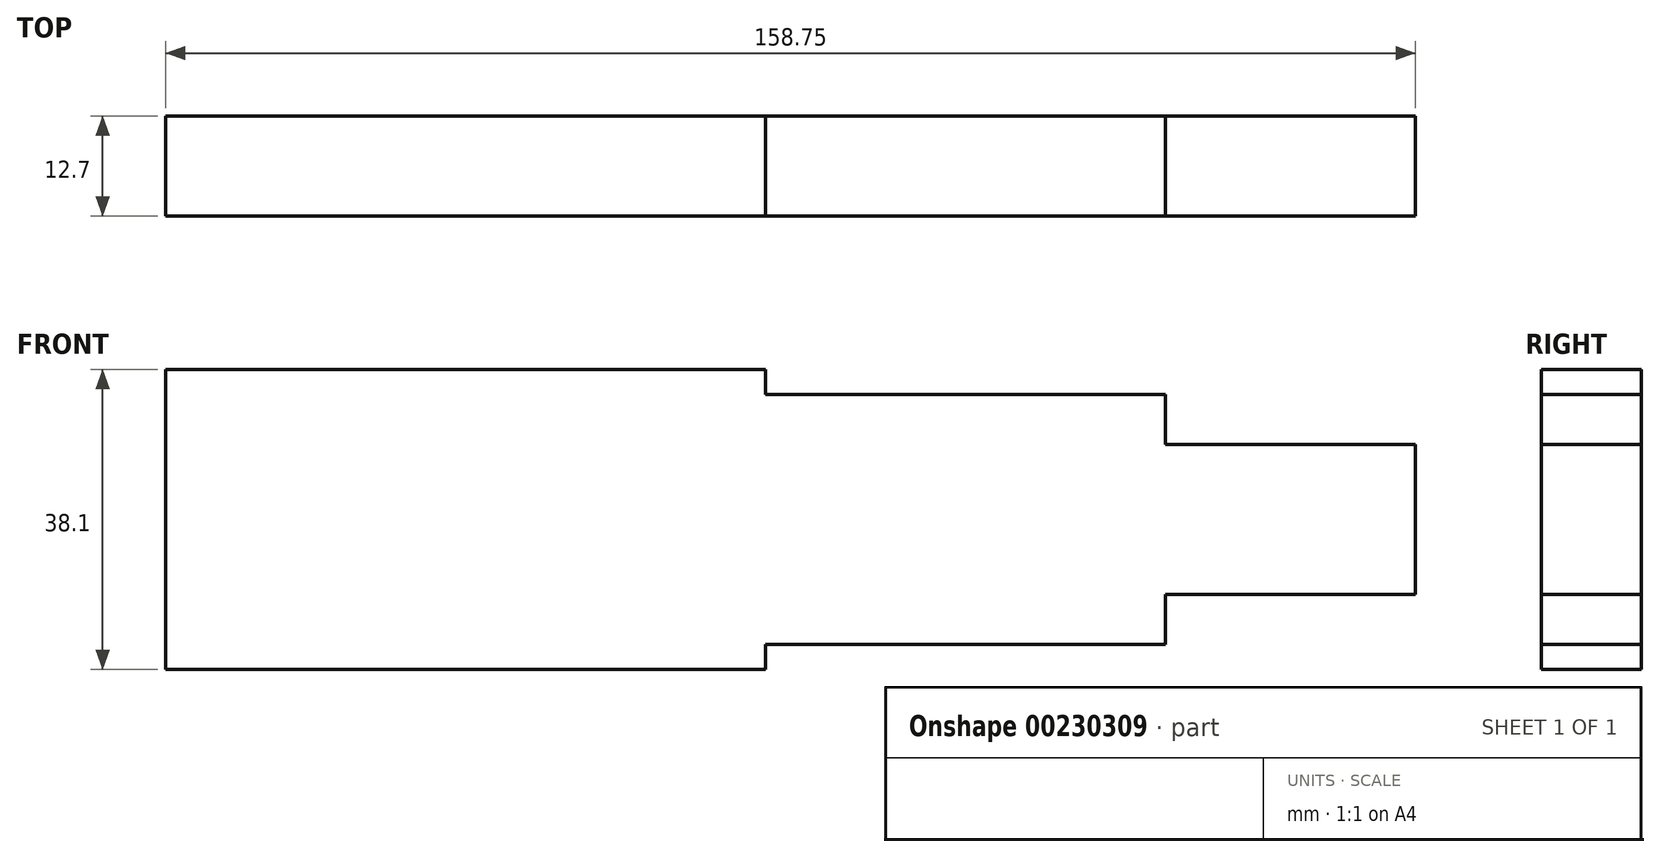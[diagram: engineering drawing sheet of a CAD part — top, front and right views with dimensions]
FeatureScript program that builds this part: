
annotation { "Feature Type Name" : "Feature", "Feature Type Description" : "" }
export const myFeature = defineFeature(function(context is Context, id is Id, definition is map)
    precondition{}
    {
        {
            var Q0;
            Q0=qCreatedBy(makeId("Front.planeOp"),FACE);
            var sketch = newSketch(context, id + "F0", { "sketchPlane" : qUnion([Q0])});
            skLineSegment(sketch, "E0.bottom", {"start": v(0, 0) * mm, "end": v(76.2, 0) * mm});
            skLineSegment(sketch, "E0.top", {"start": v(0, 38.1) * mm, "end": v(76.2, 38.1) * mm});
            skLineSegment(sketch, "E0.left", {"start": v(0, 0) * mm, "end": v(0, 38.1) * mm});
            skLineSegment(sketch, "E0.right", {"start": v(76.2, 0) * mm, "end": v(76.2, 3.17) * mm});
            skLineSegment(sketch, "E1.bottom", {"start": v(76.2, 34.93) * mm, "end": v(127, 34.93) * mm});
            skLineSegment(sketch, "E1.top", {"start": v(76.2, 3.17) * mm, "end": v(127, 3.17) * mm});
            skLineSegment(sketch, "E1.right", {"start": v(127, 34.93) * mm, "end": v(127, 28.58) * mm});
            skLineSegment(sketch, "E2.bottom", {"start": v(127, 28.58) * mm, "end": v(158.75, 28.58) * mm});
            skLineSegment(sketch, "E2.top", {"start": v(127, 9.53) * mm, "end": v(158.75, 9.53) * mm});
            skLineSegment(sketch, "E2.right", {"start": v(158.75, 28.58) * mm, "end": v(158.75, 9.53) * mm});
            skLineSegment(sketch, "E3.trimOffspring", {"start": v(76.2, 34.93) * mm, "end": v(76.2, 38.1) * mm});
            skLineSegment(sketch, "E4.trimOffspring", {"start": v(127, 9.53) * mm, "end": v(127, 3.17) * mm});
            skSolve(sketch);
        }
        {
            var Q0;
            Q0=makeQuery(id+"F0.imprint","IMPRINT",FACE,{"disambiguationData":[TD([[makeQuery(id+"F0.imprint","IMPRINT",EDGE,{"derivedFrom":sQuery(id+"F0.wireOp",EDGE,"E0.bottom")}),1.0]])]});
            extrude(context, id + "F1", {"entities" : qUnion([Q0]), "depth" : 12.7 * mm});
        }
    });
